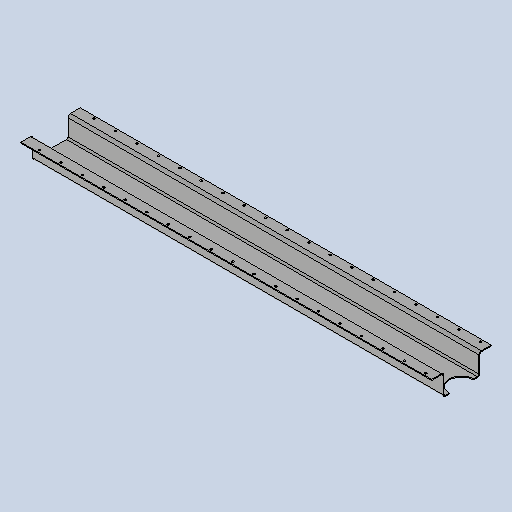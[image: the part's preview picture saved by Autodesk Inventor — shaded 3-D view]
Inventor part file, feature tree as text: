
AUTODESK INVENTOR PART (.ipt)
format: ipt  version: 2025 (Build 290162010, 162A)  size: 285,696 bytes
history: native  units: mm
features: sheet_metal_op x7, sketch x5, other x5, extrude x1, pattern_linear x1, mirror x1, projected_geometry x1
ambient origin geometry x8: Origin, YZ Plane, XZ Plane, XY Plane, X Axis, Y Axis, Z Axis, Center Point
bodies: Solid1 (feature_tree)
feature tree (21):
  sheet_metal_op  "Face1"
  sheet_metal_op  "Flange4"
  extrude  "Extrusion2"  Depth=3.0mm
  sheet_metal_op  "Flange5"
  pattern_linear  "Rectangular Pattern2"  Count1=12  [1 undecoded]
  mirror  "Mirror3"
  sketch  "Sketch1"  dims[d5=1340.0mm d6=3.0mm d30=120.0mm]
  other  "Plate1"
  sketch  "Sketch6"  dims[d60=3.0mm]
  other  "Plate5"
  sheet_metal_op  "Bend4"
  sheet_metal_op  "Corner4"
  sketch  "Sketch7"  dims[d61=1.5mm]
  sketch  "Sketch9"  dims[d62=6.0mm]
  other  "Plate6"
  sheet_metal_op  "Bend5"
  sheet_metal_op  "Corner5"
  sketch  "Sketch10"  dims[d63=5.0mm d64=70.0mm d65=90.0deg d66=5.0mm d67=12.0mm d68=3.0mm d69=5.0mm d70=80.0mm d71=0.0mm d72=0.0mm d81=3.0mm d82=1.5mm d83=6.0mm d84=5.0mm d85=40.0mm d86=90.0deg d87=5.0mm d88=12.0mm d89=3.0mm d90=5.0mm d91=7.0mm d92=27.0mm d93=3.0mm d94=0.0mm d95=300.0mm d97=70.0mm d98=8.0mm d99=10.0mm]
  projected_geometry  "Projected Loop3"
  other  "Cut1"
  other  "Definition1"
note: 1 required parameter value undecoded (feature->parameter linkage not recoverable at this tier; creation-order binding heuristic only, values carry confidence <= 0.55)
